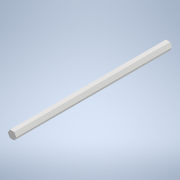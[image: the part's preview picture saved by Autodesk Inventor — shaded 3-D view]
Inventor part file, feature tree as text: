
AUTODESK INVENTOR PART (.ipt)
format: ipt  version: 2022 (Build 260153000, 153)  size: 121,856 bytes
history: native  units: mm
features: extrude x2, sketch x2
ambient origin geometry x8: Origin, YZ Plane, XZ Plane, XY Plane, X Axis, Y Axis, Z Axis, Center Point
bodies: Solid1 (feature_tree)
feature tree (4):
  extrude  "Extrusion1"  Depth=3.1mm TaperAngle=360.0deg
  extrude  "Extrusion2"  Depth=10.0mm
  sketch  "Sketch1"  dims[d0=3.1mm d1=60.0mm d3=360.0deg]
  sketch  "Sketch2"  dims[d5=115.0mm d6=0.0mm d7=1.3mm d8=5.0mm d9=60.0mm d10=3.0mm d11=10.0mm d12=0.0mm]
